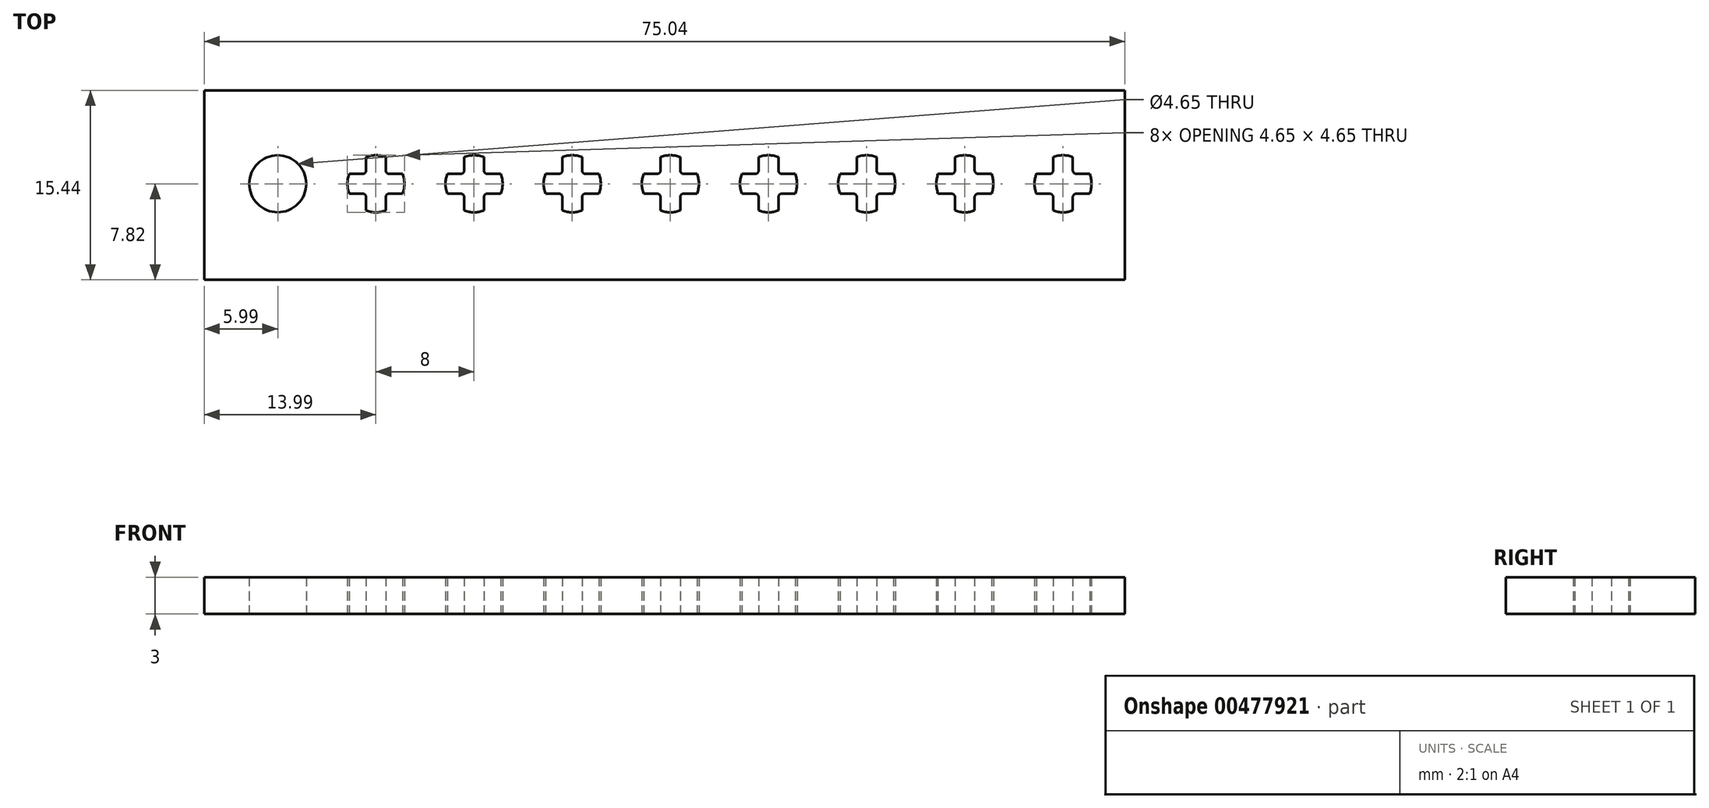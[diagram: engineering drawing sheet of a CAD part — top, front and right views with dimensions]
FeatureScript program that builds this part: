
annotation { "Feature Type Name" : "Feature", "Feature Type Description" : "" }
export const myFeature = defineFeature(function(context is Context, id is Id, definition is map)
    precondition{}
    {
        {
            var Q0;
            Q0=qCreatedBy(makeId("Top.planeOp"),FACE);
            var sketch = newSketch(context, id + "F0", { "sketchPlane" : qUnion([Q0])});
            skLineSegment(sketch, "E0", {"start": v(-0.8, 2.18) * mm, "end": v(0.8, 2.18) * mm, "construction": true});
            skLineSegment(sketch, "E1", {"start": v(2.18, 0.8) * mm, "end": v(0, 0) * mm, "construction": true});
            skLineSegment(sketch, "E2", {"start": v(0, 0) * mm, "end": v(-0.8, 2.18) * mm, "construction": true});
            skArc(sketch, "E3", {"start": v(2.18, 0.8) * mm, "mid": v(1.64, 1.64) * mm, "end": v(0.8, 2.18) * mm, "construction": true});
            skArc(sketch, "E4", {"start": v(0.8, 1.1) * mm, "mid": v(0.89, 0.89) * mm, "end": v(1.1, 0.8) * mm});
            skLineSegment(sketch, "E5", {"start": v(0.8, 2.18) * mm, "end": v(0.8, 1.1) * mm});
            skLineSegment(sketch, "E6", {"start": v(2.18, 0.8) * mm, "end": v(1.1, 0.8) * mm});
            skCircle(sketch, "E7", {"center": v(-8, 0) * mm, "radius": 2.33 * mm});
            skArc(sketch, "E8", {"start": v(0.8, 2.18) * mm, "mid": v(0, 2.32) * mm, "end": v(-0.8, 2.18) * mm});
            skArc(sketch, "E9.1.0", {"start": v(-2.18, 0.8) * mm, "mid": v(-2.32, 0) * mm, "end": v(-2.18, -0.8) * mm});
            skLineSegment(sketch, "E9.1.1", {"start": v(-2.18, 0.8) * mm, "end": v(-1.1, 0.8) * mm});
            skArc(sketch, "E9.1.2", {"start": v(-1.1, 0.8) * mm, "mid": v(-0.89, 0.89) * mm, "end": v(-0.8, 1.1) * mm});
            skLineSegment(sketch, "E9.1.3", {"start": v(-0.8, 2.18) * mm, "end": v(-0.8, 1.1) * mm});
            skArc(sketch, "E9.2.0", {"start": v(-0.8, -2.18) * mm, "mid": v(0, -2.32) * mm, "end": v(0.8, -2.18) * mm});
            skLineSegment(sketch, "E9.2.1", {"start": v(-0.8, -2.18) * mm, "end": v(-0.8, -1.1) * mm});
            skArc(sketch, "E9.2.2", {"start": v(-0.8, -1.1) * mm, "mid": v(-0.89, -0.89) * mm, "end": v(-1.1, -0.8) * mm});
            skLineSegment(sketch, "E9.2.3", {"start": v(-2.18, -0.8) * mm, "end": v(-1.1, -0.8) * mm});
            skArc(sketch, "E9.3.0", {"start": v(2.18, -0.8) * mm, "mid": v(2.32, 0) * mm, "end": v(2.18, 0.8) * mm});
            skLineSegment(sketch, "E9.3.1", {"start": v(2.18, -0.8) * mm, "end": v(1.1, -0.8) * mm});
            skArc(sketch, "E9.3.2", {"start": v(1.1, -0.8) * mm, "mid": v(0.89, -0.89) * mm, "end": v(0.8, -1.1) * mm});
            skLineSegment(sketch, "E9.3.3", {"start": v(0.8, -2.18) * mm, "end": v(0.8, -1.1) * mm});
            skArc(sketch, "E10.1.0.0", {"start": v(7.2, -2.18) * mm, "mid": v(8, -2.33) * mm, "end": v(8.8, -2.18) * mm});
            skLineSegment(sketch, "E10.1.0.1", {"start": v(8.8, 2.18) * mm, "end": v(8.8, 1.1) * mm});
            skLineSegment(sketch, "E10.1.0.2", {"start": v(7.2, 2.18) * mm, "end": v(7.2, 1.1) * mm});
            skLineSegment(sketch, "E10.1.0.3", {"start": v(10.18, 0.8) * mm, "end": v(9.1, 0.8) * mm});
            skLineSegment(sketch, "E10.1.0.4", {"start": v(7.2, -2.18) * mm, "end": v(7.2, -1.1) * mm});
            skLineSegment(sketch, "E10.1.0.5", {"start": v(8.8, -2.18) * mm, "end": v(8.8, -1.1) * mm});
            skLineSegment(sketch, "E10.1.0.6", {"start": v(10.18, -0.8) * mm, "end": v(9.1, -0.8) * mm});
            skLineSegment(sketch, "E10.1.0.7", {"start": v(10.18, 0.8) * mm, "end": v(8, 0) * mm, "construction": true});
            skArc(sketch, "E10.1.0.8", {"start": v(10.18, -0.8) * mm, "mid": v(10.33, 0) * mm, "end": v(10.18, 0.8) * mm});
            skLineSegment(sketch, "E10.1.0.9", {"start": v(7.2, 2.18) * mm, "end": v(8.8, 2.18) * mm, "construction": true});
            skPoint(sketch, "E10.1.0.10", {"position": v(8, 0) * mm});
            skArc(sketch, "E10.1.0.11", {"start": v(8.8, 2.18) * mm, "mid": v(8, 2.33) * mm, "end": v(7.2, 2.18) * mm});
            skLineSegment(sketch, "E10.1.0.12", {"start": v(5.82, 0.8) * mm, "end": v(6.9, 0.8) * mm});
            skLineSegment(sketch, "E10.1.0.13", {"start": v(5.82, -0.8) * mm, "end": v(6.9, -0.8) * mm});
            skArc(sketch, "E10.1.0.14", {"start": v(5.82, 0.8) * mm, "mid": v(5.68, 0) * mm, "end": v(5.82, -0.8) * mm});
            skLineSegment(sketch, "E10.1.0.15", {"start": v(8, 0) * mm, "end": v(7.2, 2.18) * mm, "construction": true});
            skArc(sketch, "E10.1.0.16", {"start": v(10.18, 0.8) * mm, "mid": v(9.64, 1.64) * mm, "end": v(8.8, 2.18) * mm, "construction": true});
            skArc(sketch, "E10.1.0.17", {"start": v(9.1, -0.8) * mm, "mid": v(8.89, -0.89) * mm, "end": v(8.8, -1.1) * mm});
            skArc(sketch, "E10.1.0.18", {"start": v(7.2, -1.1) * mm, "mid": v(7.11, -0.89) * mm, "end": v(6.9, -0.8) * mm});
            skArc(sketch, "E10.1.0.19", {"start": v(6.9, 0.8) * mm, "mid": v(7.11, 0.89) * mm, "end": v(7.2, 1.1) * mm});
            skArc(sketch, "E10.1.0.20", {"start": v(8.8, 1.1) * mm, "mid": v(8.89, 0.89) * mm, "end": v(9.1, 0.8) * mm});
            skArc(sketch, "E10.2.0.0", {"start": v(15.2, -2.18) * mm, "mid": v(16, -2.33) * mm, "end": v(16.8, -2.18) * mm});
            skLineSegment(sketch, "E10.2.0.1", {"start": v(16.8, 2.18) * mm, "end": v(16.8, 1.1) * mm});
            skLineSegment(sketch, "E10.2.0.2", {"start": v(15.2, 2.18) * mm, "end": v(15.2, 1.1) * mm});
            skLineSegment(sketch, "E10.2.0.3", {"start": v(18.18, 0.8) * mm, "end": v(17.1, 0.8) * mm});
            skLineSegment(sketch, "E10.2.0.4", {"start": v(15.2, -2.18) * mm, "end": v(15.2, -1.1) * mm});
            skLineSegment(sketch, "E10.2.0.5", {"start": v(16.8, -2.18) * mm, "end": v(16.8, -1.1) * mm});
            skLineSegment(sketch, "E10.2.0.6", {"start": v(18.18, -0.8) * mm, "end": v(17.1, -0.8) * mm});
            skLineSegment(sketch, "E10.2.0.7", {"start": v(18.18, 0.8) * mm, "end": v(16, 0) * mm, "construction": true});
            skArc(sketch, "E10.2.0.8", {"start": v(18.18, -0.8) * mm, "mid": v(18.32, 0) * mm, "end": v(18.18, 0.8) * mm});
            skLineSegment(sketch, "E10.2.0.9", {"start": v(15.2, 2.18) * mm, "end": v(16.8, 2.18) * mm, "construction": true});
            skPoint(sketch, "E10.2.0.10", {"position": v(16, 0) * mm});
            skArc(sketch, "E10.2.0.11", {"start": v(16.8, 2.18) * mm, "mid": v(16, 2.33) * mm, "end": v(15.2, 2.18) * mm});
            skLineSegment(sketch, "E10.2.0.12", {"start": v(13.82, 0.8) * mm, "end": v(14.9, 0.8) * mm});
            skLineSegment(sketch, "E10.2.0.13", {"start": v(13.82, -0.8) * mm, "end": v(14.9, -0.8) * mm});
            skArc(sketch, "E10.2.0.14", {"start": v(13.82, 0.8) * mm, "mid": v(13.67, 0) * mm, "end": v(13.82, -0.8) * mm});
            skLineSegment(sketch, "E10.2.0.15", {"start": v(16, 0) * mm, "end": v(15.2, 2.18) * mm, "construction": true});
            skArc(sketch, "E10.2.0.16", {"start": v(18.18, 0.8) * mm, "mid": v(17.64, 1.64) * mm, "end": v(16.8, 2.18) * mm, "construction": true});
            skArc(sketch, "E10.2.0.17", {"start": v(17.1, -0.8) * mm, "mid": v(16.89, -0.89) * mm, "end": v(16.8, -1.1) * mm});
            skArc(sketch, "E10.2.0.18", {"start": v(15.2, -1.1) * mm, "mid": v(15.11, -0.89) * mm, "end": v(14.9, -0.8) * mm});
            skArc(sketch, "E10.2.0.19", {"start": v(14.9, 0.8) * mm, "mid": v(15.11, 0.89) * mm, "end": v(15.2, 1.1) * mm});
            skArc(sketch, "E10.2.0.20", {"start": v(16.8, 1.1) * mm, "mid": v(16.89, 0.89) * mm, "end": v(17.1, 0.8) * mm});
            skArc(sketch, "E10.3.0.0", {"start": v(23.2, -2.18) * mm, "mid": v(24, -2.33) * mm, "end": v(24.8, -2.18) * mm});
            skLineSegment(sketch, "E10.3.0.1", {"start": v(24.8, 2.18) * mm, "end": v(24.8, 1.1) * mm});
            skLineSegment(sketch, "E10.3.0.2", {"start": v(23.2, 2.18) * mm, "end": v(23.2, 1.1) * mm});
            skLineSegment(sketch, "E10.3.0.3", {"start": v(26.18, 0.8) * mm, "end": v(25.1, 0.8) * mm});
            skLineSegment(sketch, "E10.3.0.4", {"start": v(23.2, -2.18) * mm, "end": v(23.2, -1.1) * mm});
            skLineSegment(sketch, "E10.3.0.5", {"start": v(24.8, -2.18) * mm, "end": v(24.8, -1.1) * mm});
            skLineSegment(sketch, "E10.3.0.6", {"start": v(26.18, -0.8) * mm, "end": v(25.1, -0.8) * mm});
            skLineSegment(sketch, "E10.3.0.7", {"start": v(26.18, 0.8) * mm, "end": v(24, 0) * mm, "construction": true});
            skArc(sketch, "E10.3.0.8", {"start": v(26.18, -0.8) * mm, "mid": v(26.33, 0) * mm, "end": v(26.18, 0.8) * mm});
            skLineSegment(sketch, "E10.3.0.9", {"start": v(23.2, 2.18) * mm, "end": v(24.8, 2.18) * mm, "construction": true});
            skPoint(sketch, "E10.3.0.10", {"position": v(24, 0) * mm});
            skArc(sketch, "E10.3.0.11", {"start": v(24.8, 2.18) * mm, "mid": v(24, 2.33) * mm, "end": v(23.2, 2.18) * mm});
            skLineSegment(sketch, "E10.3.0.12", {"start": v(21.82, 0.8) * mm, "end": v(22.9, 0.8) * mm});
            skLineSegment(sketch, "E10.3.0.13", {"start": v(21.82, -0.8) * mm, "end": v(22.9, -0.8) * mm});
            skArc(sketch, "E10.3.0.14", {"start": v(21.82, 0.8) * mm, "mid": v(21.68, 0) * mm, "end": v(21.82, -0.8) * mm});
            skLineSegment(sketch, "E10.3.0.15", {"start": v(24, 0) * mm, "end": v(23.2, 2.18) * mm, "construction": true});
            skArc(sketch, "E10.3.0.16", {"start": v(26.18, 0.8) * mm, "mid": v(25.64, 1.64) * mm, "end": v(24.8, 2.18) * mm, "construction": true});
            skArc(sketch, "E10.3.0.17", {"start": v(25.1, -0.8) * mm, "mid": v(24.89, -0.89) * mm, "end": v(24.8, -1.1) * mm});
            skArc(sketch, "E10.3.0.18", {"start": v(23.2, -1.1) * mm, "mid": v(23.11, -0.89) * mm, "end": v(22.9, -0.8) * mm});
            skArc(sketch, "E10.3.0.19", {"start": v(22.9, 0.8) * mm, "mid": v(23.11, 0.89) * mm, "end": v(23.2, 1.1) * mm});
            skArc(sketch, "E10.3.0.20", {"start": v(24.8, 1.1) * mm, "mid": v(24.89, 0.89) * mm, "end": v(25.1, 0.8) * mm});
            skArc(sketch, "E10.4.0.0", {"start": v(31.2, -2.18) * mm, "mid": v(32, -2.33) * mm, "end": v(32.8, -2.18) * mm});
            skLineSegment(sketch, "E10.4.0.1", {"start": v(32.8, 2.18) * mm, "end": v(32.8, 1.1) * mm});
            skLineSegment(sketch, "E10.4.0.2", {"start": v(31.2, 2.18) * mm, "end": v(31.2, 1.1) * mm});
            skLineSegment(sketch, "E10.4.0.3", {"start": v(34.18, 0.8) * mm, "end": v(33.1, 0.8) * mm});
            skLineSegment(sketch, "E10.4.0.4", {"start": v(31.2, -2.18) * mm, "end": v(31.2, -1.1) * mm});
            skLineSegment(sketch, "E10.4.0.5", {"start": v(32.8, -2.18) * mm, "end": v(32.8, -1.1) * mm});
            skLineSegment(sketch, "E10.4.0.6", {"start": v(34.18, -0.8) * mm, "end": v(33.1, -0.8) * mm});
            skLineSegment(sketch, "E10.4.0.7", {"start": v(34.18, 0.8) * mm, "end": v(32, 0) * mm, "construction": true});
            skArc(sketch, "E10.4.0.8", {"start": v(34.18, -0.8) * mm, "mid": v(34.33, 0) * mm, "end": v(34.18, 0.8) * mm});
            skLineSegment(sketch, "E10.4.0.9", {"start": v(31.2, 2.18) * mm, "end": v(32.8, 2.18) * mm, "construction": true});
            skPoint(sketch, "E10.4.0.10", {"position": v(32, 0) * mm});
            skArc(sketch, "E10.4.0.11", {"start": v(32.8, 2.18) * mm, "mid": v(32, 2.33) * mm, "end": v(31.2, 2.18) * mm});
            skLineSegment(sketch, "E10.4.0.12", {"start": v(29.82, 0.8) * mm, "end": v(30.9, 0.8) * mm});
            skLineSegment(sketch, "E10.4.0.13", {"start": v(29.82, -0.8) * mm, "end": v(30.9, -0.8) * mm});
            skArc(sketch, "E10.4.0.14", {"start": v(29.82, 0.8) * mm, "mid": v(29.68, 0) * mm, "end": v(29.82, -0.8) * mm});
            skLineSegment(sketch, "E10.4.0.15", {"start": v(32, 0) * mm, "end": v(31.2, 2.18) * mm, "construction": true});
            skArc(sketch, "E10.4.0.16", {"start": v(34.18, 0.8) * mm, "mid": v(33.64, 1.64) * mm, "end": v(32.8, 2.18) * mm, "construction": true});
            skArc(sketch, "E10.4.0.17", {"start": v(33.1, -0.8) * mm, "mid": v(32.89, -0.89) * mm, "end": v(32.8, -1.1) * mm});
            skArc(sketch, "E10.4.0.18", {"start": v(31.2, -1.1) * mm, "mid": v(31.11, -0.89) * mm, "end": v(30.9, -0.8) * mm});
            skArc(sketch, "E10.4.0.19", {"start": v(30.9, 0.8) * mm, "mid": v(31.11, 0.89) * mm, "end": v(31.2, 1.1) * mm});
            skArc(sketch, "E10.4.0.20", {"start": v(32.8, 1.1) * mm, "mid": v(32.89, 0.89) * mm, "end": v(33.1, 0.8) * mm});
            skArc(sketch, "E10.5.0.0", {"start": v(39.2, -2.18) * mm, "mid": v(40, -2.33) * mm, "end": v(40.8, -2.18) * mm});
            skLineSegment(sketch, "E10.5.0.1", {"start": v(40.8, 2.18) * mm, "end": v(40.8, 1.1) * mm});
            skLineSegment(sketch, "E10.5.0.2", {"start": v(39.2, 2.18) * mm, "end": v(39.2, 1.1) * mm});
            skLineSegment(sketch, "E10.5.0.3", {"start": v(42.18, 0.8) * mm, "end": v(41.1, 0.8) * mm});
            skLineSegment(sketch, "E10.5.0.4", {"start": v(39.2, -2.18) * mm, "end": v(39.2, -1.1) * mm});
            skLineSegment(sketch, "E10.5.0.5", {"start": v(40.8, -2.18) * mm, "end": v(40.8, -1.1) * mm});
            skLineSegment(sketch, "E10.5.0.6", {"start": v(42.18, -0.8) * mm, "end": v(41.1, -0.8) * mm});
            skLineSegment(sketch, "E10.5.0.7", {"start": v(42.18, 0.8) * mm, "end": v(40, 0) * mm, "construction": true});
            skArc(sketch, "E10.5.0.8", {"start": v(42.18, -0.8) * mm, "mid": v(42.33, 0) * mm, "end": v(42.18, 0.8) * mm});
            skLineSegment(sketch, "E10.5.0.9", {"start": v(39.2, 2.18) * mm, "end": v(40.8, 2.18) * mm, "construction": true});
            skPoint(sketch, "E10.5.0.10", {"position": v(40, 0) * mm});
            skArc(sketch, "E10.5.0.11", {"start": v(40.8, 2.18) * mm, "mid": v(40, 2.33) * mm, "end": v(39.2, 2.18) * mm});
            skLineSegment(sketch, "E10.5.0.12", {"start": v(37.82, 0.8) * mm, "end": v(38.9, 0.8) * mm});
            skLineSegment(sketch, "E10.5.0.13", {"start": v(37.82, -0.8) * mm, "end": v(38.9, -0.8) * mm});
            skArc(sketch, "E10.5.0.14", {"start": v(37.82, 0.8) * mm, "mid": v(37.67, 0) * mm, "end": v(37.82, -0.8) * mm});
            skLineSegment(sketch, "E10.5.0.15", {"start": v(40, 0) * mm, "end": v(39.2, 2.18) * mm, "construction": true});
            skArc(sketch, "E10.5.0.16", {"start": v(42.18, 0.8) * mm, "mid": v(41.64, 1.64) * mm, "end": v(40.8, 2.18) * mm, "construction": true});
            skArc(sketch, "E10.5.0.17", {"start": v(41.1, -0.8) * mm, "mid": v(40.89, -0.89) * mm, "end": v(40.8, -1.1) * mm});
            skArc(sketch, "E10.5.0.18", {"start": v(39.2, -1.1) * mm, "mid": v(39.11, -0.89) * mm, "end": v(38.9, -0.8) * mm});
            skArc(sketch, "E10.5.0.19", {"start": v(38.9, 0.8) * mm, "mid": v(39.11, 0.89) * mm, "end": v(39.2, 1.1) * mm});
            skArc(sketch, "E10.5.0.20", {"start": v(40.8, 1.1) * mm, "mid": v(40.89, 0.89) * mm, "end": v(41.1, 0.8) * mm});
            skArc(sketch, "E10.6.0.0", {"start": v(47.2, -2.18) * mm, "mid": v(48, -2.33) * mm, "end": v(48.8, -2.18) * mm});
            skLineSegment(sketch, "E10.6.0.1", {"start": v(48.8, 2.18) * mm, "end": v(48.8, 1.1) * mm});
            skLineSegment(sketch, "E10.6.0.2", {"start": v(47.2, 2.18) * mm, "end": v(47.2, 1.1) * mm});
            skLineSegment(sketch, "E10.6.0.3", {"start": v(50.18, 0.8) * mm, "end": v(49.1, 0.8) * mm});
            skLineSegment(sketch, "E10.6.0.4", {"start": v(47.2, -2.18) * mm, "end": v(47.2, -1.1) * mm});
            skLineSegment(sketch, "E10.6.0.5", {"start": v(48.8, -2.18) * mm, "end": v(48.8, -1.1) * mm});
            skLineSegment(sketch, "E10.6.0.6", {"start": v(50.18, -0.8) * mm, "end": v(49.1, -0.8) * mm});
            skLineSegment(sketch, "E10.6.0.7", {"start": v(50.18, 0.8) * mm, "end": v(48, 0) * mm, "construction": true});
            skArc(sketch, "E10.6.0.8", {"start": v(50.18, -0.8) * mm, "mid": v(50.33, 0) * mm, "end": v(50.18, 0.8) * mm});
            skLineSegment(sketch, "E10.6.0.9", {"start": v(47.2, 2.18) * mm, "end": v(48.8, 2.18) * mm, "construction": true});
            skPoint(sketch, "E10.6.0.10", {"position": v(48, 0) * mm});
            skArc(sketch, "E10.6.0.11", {"start": v(48.8, 2.18) * mm, "mid": v(48, 2.33) * mm, "end": v(47.2, 2.18) * mm});
            skLineSegment(sketch, "E10.6.0.12", {"start": v(45.82, 0.8) * mm, "end": v(46.9, 0.8) * mm});
            skLineSegment(sketch, "E10.6.0.13", {"start": v(45.82, -0.8) * mm, "end": v(46.9, -0.8) * mm});
            skArc(sketch, "E10.6.0.14", {"start": v(45.82, 0.8) * mm, "mid": v(45.67, 0) * mm, "end": v(45.82, -0.8) * mm});
            skLineSegment(sketch, "E10.6.0.15", {"start": v(48, 0) * mm, "end": v(47.2, 2.18) * mm, "construction": true});
            skArc(sketch, "E10.6.0.16", {"start": v(50.18, 0.8) * mm, "mid": v(49.64, 1.64) * mm, "end": v(48.8, 2.18) * mm, "construction": true});
            skArc(sketch, "E10.6.0.17", {"start": v(49.1, -0.8) * mm, "mid": v(48.89, -0.89) * mm, "end": v(48.8, -1.1) * mm});
            skArc(sketch, "E10.6.0.18", {"start": v(47.2, -1.1) * mm, "mid": v(47.11, -0.89) * mm, "end": v(46.9, -0.8) * mm});
            skArc(sketch, "E10.6.0.19", {"start": v(46.9, 0.8) * mm, "mid": v(47.11, 0.89) * mm, "end": v(47.2, 1.1) * mm});
            skArc(sketch, "E10.6.0.20", {"start": v(48.8, 1.1) * mm, "mid": v(48.89, 0.89) * mm, "end": v(49.1, 0.8) * mm});
            skArc(sketch, "E10.7.0.0", {"start": v(55.2, -2.18) * mm, "mid": v(56, -2.33) * mm, "end": v(56.8, -2.18) * mm});
            skLineSegment(sketch, "E10.7.0.1", {"start": v(56.8, 2.18) * mm, "end": v(56.8, 1.1) * mm});
            skLineSegment(sketch, "E10.7.0.2", {"start": v(55.2, 2.18) * mm, "end": v(55.2, 1.1) * mm});
            skLineSegment(sketch, "E10.7.0.3", {"start": v(58.18, 0.8) * mm, "end": v(57.1, 0.8) * mm});
            skLineSegment(sketch, "E10.7.0.4", {"start": v(55.2, -2.18) * mm, "end": v(55.2, -1.1) * mm});
            skLineSegment(sketch, "E10.7.0.5", {"start": v(56.8, -2.18) * mm, "end": v(56.8, -1.1) * mm});
            skLineSegment(sketch, "E10.7.0.6", {"start": v(58.18, -0.8) * mm, "end": v(57.1, -0.8) * mm});
            skLineSegment(sketch, "E10.7.0.7", {"start": v(58.18, 0.8) * mm, "end": v(56, 0) * mm, "construction": true});
            skArc(sketch, "E10.7.0.8", {"start": v(58.18, -0.8) * mm, "mid": v(58.33, 0) * mm, "end": v(58.18, 0.8) * mm});
            skLineSegment(sketch, "E10.7.0.9", {"start": v(55.2, 2.18) * mm, "end": v(56.8, 2.18) * mm, "construction": true});
            skPoint(sketch, "E10.7.0.10", {"position": v(56, 0) * mm});
            skArc(sketch, "E10.7.0.11", {"start": v(56.8, 2.18) * mm, "mid": v(56, 2.33) * mm, "end": v(55.2, 2.18) * mm});
            skLineSegment(sketch, "E10.7.0.12", {"start": v(53.82, 0.8) * mm, "end": v(54.9, 0.8) * mm});
            skLineSegment(sketch, "E10.7.0.13", {"start": v(53.82, -0.8) * mm, "end": v(54.9, -0.8) * mm});
            skArc(sketch, "E10.7.0.14", {"start": v(53.82, 0.8) * mm, "mid": v(53.67, 0) * mm, "end": v(53.82, -0.8) * mm});
            skLineSegment(sketch, "E10.7.0.15", {"start": v(56, 0) * mm, "end": v(55.2, 2.18) * mm, "construction": true});
            skArc(sketch, "E10.7.0.16", {"start": v(58.18, 0.8) * mm, "mid": v(57.64, 1.64) * mm, "end": v(56.8, 2.18) * mm, "construction": true});
            skArc(sketch, "E10.7.0.17", {"start": v(57.1, -0.8) * mm, "mid": v(56.89, -0.89) * mm, "end": v(56.8, -1.1) * mm});
            skArc(sketch, "E10.7.0.18", {"start": v(55.2, -1.1) * mm, "mid": v(55.11, -0.89) * mm, "end": v(54.9, -0.8) * mm});
            skArc(sketch, "E10.7.0.19", {"start": v(54.9, 0.8) * mm, "mid": v(55.11, 0.89) * mm, "end": v(55.2, 1.1) * mm});
            skArc(sketch, "E10.7.0.20", {"start": v(56.8, 1.1) * mm, "mid": v(56.89, 0.89) * mm, "end": v(57.1, 0.8) * mm});
            skLineSegment(sketch, "E10.direction1", {"start": v(-0.8, -2.18) * mm, "end": v(7.2, -2.18) * mm, "construction": true});
            skLineSegment(sketch, "E11.bottom", {"start": v(-13.99, 7.62) * mm, "end": v(61.05, 7.62) * mm});
            skLineSegment(sketch, "E11.top", {"start": v(-13.99, -7.82) * mm, "end": v(61.05, -7.82) * mm});
            skLineSegment(sketch, "E11.left", {"start": v(-13.99, 7.62) * mm, "end": v(-13.99, -7.82) * mm});
            skLineSegment(sketch, "E11.right", {"start": v(61.05, 7.62) * mm, "end": v(61.05, -7.82) * mm});
            skSolve(sketch);
        }
        {
            var Q0;
            Q0 = qSketchRegion(id + "F0", true);
            extrude(context, id + "F1", {"entities" : qUnion([Q0]), "depth" : 3 * mm, "offsetDistance" : 25 * mm});
        }
    });
